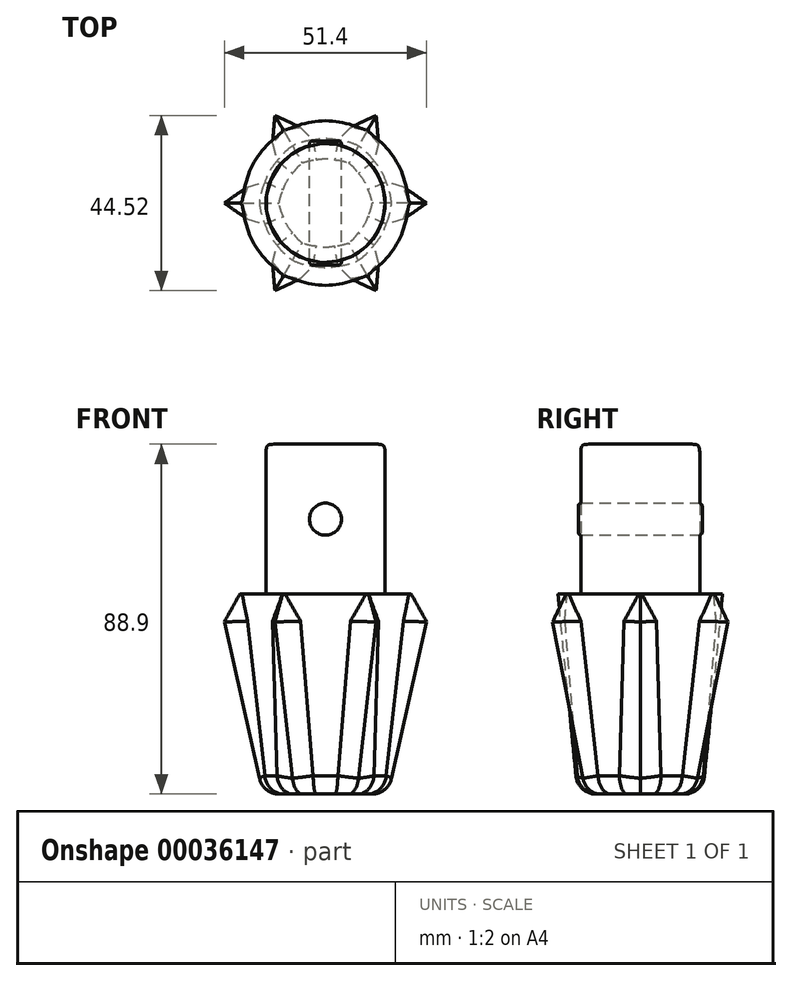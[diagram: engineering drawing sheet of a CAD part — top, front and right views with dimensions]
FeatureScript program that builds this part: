
annotation { "Feature Type Name" : "Feature", "Feature Type Description" : "" }
export const myFeature = defineFeature(function(context is Context, id is Id, definition is map)
    precondition{}
    {
        {
            var Q0;
            Q0=qCreatedBy(makeId("Top.planeOp"),FACE);
            cPlane(context, id + "F0", {"entities" : qUnion([Q0]), "cplaneType" : CPlaneType.OFFSET, "offset" : 50.8 * mm, "width" : 152.4 * mm, "height" : 152.4 * mm});
        }
        {
            var Q0;
            Q0=qCreatedBy(id+"F0.planeOp",FACE);
            var sketch = newSketch(context, id + "F1", { "sketchPlane" : qUnion([Q0])});
            skCircle(sketch, "E0.cCircle", {"center": v(0, 0) * mm, "radius": 27.3 * mm, "construction": true});
            skLineSegment(sketch, "E0.0", {"start": v(13.65, 23.64) * mm, "end": v(13.65, 15.82) * mm});
            skLineSegment(sketch, "E0.1", {"start": v(13.65, -23.64) * mm, "end": v(6.88, -19.73) * mm});
            skLineSegment(sketch, "E0.2", {"start": v(-27.3, 0) * mm, "end": v(-20.53, 3.9) * mm});
            skLineSegment(sketch, "E1.0", {"start": v(-13.65, 23.64) * mm, "end": v(-6.88, 19.73) * mm});
            skLineSegment(sketch, "E1.1", {"start": v(27.3, 0) * mm, "end": v(20.53, -3.9) * mm});
            skLineSegment(sketch, "E1.2", {"start": v(-13.65, -23.64) * mm, "end": v(-13.65, -15.82) * mm});
            skArc(sketch, "E2", {"start": v(-13.65, 15.82) * mm, "mid": v(-18.1, 10.45) * mm, "end": v(-20.53, 3.9) * mm});
            skLineSegment(sketch, "E3.trimOffspring", {"start": v(20.53, 3.9) * mm, "end": v(27.3, 0) * mm});
            skLineSegment(sketch, "E4.trimOffspring", {"start": v(-13.65, 15.82) * mm, "end": v(-13.65, 23.64) * mm});
            skLineSegment(sketch, "E5.trimOffspring", {"start": v(6.88, 19.73) * mm, "end": v(13.65, 23.64) * mm});
            skArc(sketch, "E6.trimOffspring", {"start": v(-20.53, -3.9) * mm, "mid": v(-18.1, -10.45) * mm, "end": v(-13.65, -15.82) * mm});
            skLineSegment(sketch, "E7.trimOffspring", {"start": v(-20.53, -3.9) * mm, "end": v(-27.3, 0) * mm});
            skArc(sketch, "E8.trimOffspring", {"start": v(-6.88, -19.73) * mm, "mid": v(0, -20.9) * mm, "end": v(6.88, -19.73) * mm});
            skArc(sketch, "E9.trimOffspring", {"start": v(13.65, -15.82) * mm, "mid": v(18.1, -10.45) * mm, "end": v(20.53, -3.9) * mm});
            skArc(sketch, "E10.trimOffspring", {"start": v(20.53, 3.9) * mm, "mid": v(18.1, 10.45) * mm, "end": v(13.65, 15.82) * mm});
            skArc(sketch, "E11.trimOffspring", {"start": v(6.88, 19.73) * mm, "mid": v(0, 20.9) * mm, "end": v(-6.88, 19.73) * mm});
            skLineSegment(sketch, "E12.trimOffspring", {"start": v(13.65, -15.82) * mm, "end": v(13.65, -23.64) * mm});
            skLineSegment(sketch, "E13.trimOffspring", {"start": v(-6.88, -19.73) * mm, "end": v(-13.65, -23.64) * mm});
            skSolve(sketch);
        }
        {
            var Q0;
            Q0=qCreatedBy(makeId("Top.planeOp"),FACE);
            var sketch = newSketch(context, id + "F2", { "sketchPlane" : qUnion([Q0])});
            skCircle(sketch, "E14", {"center": v(0, 0) * mm, "radius": 15.88 * mm});
            skSolve(sketch);
        }
        {
            var Q0;
            Q0=makeQuery(id+"F1.imprint","IMPRINT",FACE,{"disambiguationData":[TD([[makeQuery(id+"F1.imprint","IMPRINT",EDGE,{"derivedFrom":sQuery(id+"F1.wireOp",EDGE,"E0.0")}),-1.0]])]});
            var Q1;
            Q1=makeQuery(id+"F2.imprint","IMPRINT",FACE,{"disambiguationData":[TD([[makeQuery(id+"F2.imprint","IMPRINT",EDGE,{"derivedFrom":sQuery(id+"F2.wireOp",EDGE,"E14")}),1.0]])]});
            loft(context, id + "F3", {"sheetProfilesArray" : [{ "sheetProfileEntities" : qUnion([Q0]) }, { "sheetProfileEntities" : qUnion([Q1]) }]});
        }
        {
            var Q0;
            Q0=makeQuery(id+"F3.opLoft","CAP_FACE",FACE,{"disambiguationData":[OSD([makeQuery(id+"F2.imprint","IMPRINT",FACE,{"disambiguationData":[TD([[makeQuery(id+"F2.imprint","IMPRINT",EDGE,{"derivedFrom":sQuery(id+"F2.wireOp",EDGE,"E14")}),1.0]])]})])],"isStart":true});
            fillet(context, id + "F4", {"entities" : qUnion([Q0]), "radius" : 5.08 * mm, "tangentPropagation" : true, "allowEdgeOverflow" : false});
        }
        {
            var Q0;
            Q0=makeQuery(id+"F3.opLoft","MID_CAP_EDGE",EDGE,{"disambiguationData":[OSD([sQuery(id+"F1.wireOp",EDGE,"E0.1"),sQuery(id+"F1.wireOp",EDGE,"E9.trimOffspring"),sQuery(id+"F1.wireOp",EDGE,"E12.trimOffspring")])],"capPos":0.0});
            var Q1;
            Q1=makeQuery(id+"F3.opLoft","MID_CAP_EDGE",EDGE,{"disambiguationData":[OSD([sQuery(id+"F1.wireOp",EDGE,"E0.1"),sQuery(id+"F1.wireOp",EDGE,"E8.trimOffspring"),sQuery(id+"F1.wireOp",EDGE,"E12.trimOffspring")])],"capPos":0.0});
            var Q2;
            Q2=makeQuery(id+"F3.opLoft","MID_CAP_EDGE",EDGE,{"disambiguationData":[OSD([sQuery(id+"F1.wireOp",EDGE,"E1.1"),sQuery(id+"F1.wireOp",EDGE,"E3.trimOffspring"),sQuery(id+"F1.wireOp",EDGE,"E9.trimOffspring")])],"capPos":0.0});
            var Q3;
            Q3=makeQuery(id+"F3.opLoft","MID_CAP_EDGE",EDGE,{"disambiguationData":[OSD([sQuery(id+"F1.wireOp",EDGE,"E1.1"),sQuery(id+"F1.wireOp",EDGE,"E3.trimOffspring"),sQuery(id+"F1.wireOp",EDGE,"E10.trimOffspring")])],"capPos":0.0});
            var Q4;
            Q4=makeQuery(id+"F3.opLoft","MID_CAP_EDGE",EDGE,{"disambiguationData":[OSD([sQuery(id+"F1.wireOp",EDGE,"E0.0"),sQuery(id+"F1.wireOp",EDGE,"E5.trimOffspring"),sQuery(id+"F1.wireOp",EDGE,"E11.trimOffspring")])],"capPos":0.0});
            var Q5;
            Q5=makeQuery(id+"F3.opLoft","MID_CAP_EDGE",EDGE,{"disambiguationData":[OSD([sQuery(id+"F1.wireOp",EDGE,"E1.0"),sQuery(id+"F1.wireOp",EDGE,"E2"),sQuery(id+"F1.wireOp",EDGE,"E4.trimOffspring")])],"capPos":0.0});
            var Q6;
            Q6=makeQuery(id+"F3.opLoft","MID_CAP_EDGE",EDGE,{"disambiguationData":[OSD([sQuery(id+"F1.wireOp",EDGE,"E1.0"),sQuery(id+"F1.wireOp",EDGE,"E4.trimOffspring"),sQuery(id+"F1.wireOp",EDGE,"E11.trimOffspring")])],"capPos":0.0});
            var Q7;
            Q7=makeQuery(id+"F3.opLoft","MID_CAP_EDGE",EDGE,{"disambiguationData":[OSD([sQuery(id+"F1.wireOp",EDGE,"E0.0"),sQuery(id+"F1.wireOp",EDGE,"E5.trimOffspring"),sQuery(id+"F1.wireOp",EDGE,"E10.trimOffspring")])],"capPos":0.0});
            var Q8;
            Q8=makeQuery(id+"F3.opLoft","MID_CAP_EDGE",EDGE,{"disambiguationData":[OSD([sQuery(id+"F1.wireOp",EDGE,"E0.2"),sQuery(id+"F1.wireOp",EDGE,"E2"),sQuery(id+"F1.wireOp",EDGE,"E7.trimOffspring")])],"capPos":0.0});
            var Q9;
            Q9=makeQuery(id+"F3.opLoft","MID_CAP_EDGE",EDGE,{"disambiguationData":[OSD([sQuery(id+"F1.wireOp",EDGE,"E0.2"),sQuery(id+"F1.wireOp",EDGE,"E6.trimOffspring"),sQuery(id+"F1.wireOp",EDGE,"E7.trimOffspring")])],"capPos":0.0});
            var Q10;
            Q10=makeQuery(id+"F3.opLoft","MID_CAP_EDGE",EDGE,{"disambiguationData":[OSD([sQuery(id+"F1.wireOp",EDGE,"E1.2"),sQuery(id+"F1.wireOp",EDGE,"E6.trimOffspring"),sQuery(id+"F1.wireOp",EDGE,"E13.trimOffspring")])],"capPos":0.0});
            var Q11;
            Q11=makeQuery(id+"F3.opLoft","MID_CAP_EDGE",EDGE,{"disambiguationData":[OSD([sQuery(id+"F1.wireOp",EDGE,"E1.2"),sQuery(id+"F1.wireOp",EDGE,"E8.trimOffspring"),sQuery(id+"F1.wireOp",EDGE,"E13.trimOffspring")])],"capPos":0.0});
            chamfer(context, id + "F5", {"entities" : qUnion([Q0, Q1, Q2, Q3, Q4, Q5, Q6, Q7, Q8, Q9, Q10, Q11]), "chamferType" : ChamferType.OFFSET_ANGLE, "width" : 6.86 * mm, "oppositeDirection" : false, "angle" : 20 * degree, "tangentPropagation" : true});
        }
        {
            var Q0;
            Q0=makeQuery(id+"F3.opLoft","CAP_FACE",FACE,{"disambiguationData":[OSD([makeQuery(id+"F1.imprint","IMPRINT",FACE,{"disambiguationData":[TD([[makeQuery(id+"F1.imprint","IMPRINT",EDGE,{"derivedFrom":sQuery(id+"F1.wireOp",EDGE,"E0.0")}),-1.0]])]})])],"isStart":true});
            var sketch = newSketch(context, id + "F6", { "sketchPlane" : qUnion([Q0])});
            skCircle(sketch, "E15", {"center": v(0, 0) * mm, "radius": 15.11 * mm});
            skSolve(sketch);
        }
        {
            var Q0;
            Q0=makeQuery(id+"F6.imprint","IMPRINT",FACE,{"disambiguationData":[TD([[makeQuery(id+"F6.imprint","IMPRINT",EDGE,{"derivedFrom":sQuery(id+"F6.wireOp",EDGE,"E15")}),1.0]])]});
            extrude(context, id + "F7", {"entities" : qUnion([Q0]), "operationType" : NewBodyOperationType.ADD, "depth" : 38.1 * mm});
        }
        {
            var Q0;
            Q0=makeQuery(id+"F7.opExtrude","CAP_EDGE",EDGE,{"disambiguationData":[OSD([sQuery(id+"F6.wireOp",EDGE,"E15")])],"isStart":false});
            fillet(context, id + "F8", {"entities" : qUnion([Q0]), "radius" : 2.54 * mm, "tangentPropagation" : true, "rho" : 0.7, "crossSection" : FilletCrossSection.CONIC, "allowEdgeOverflow" : false});
        }
        {
            var Q0;
            Q0=qCreatedBy(makeId("Front.planeOp"),FACE);
            var sketch = newSketch(context, id + "F9", { "sketchPlane" : qUnion([Q0])});
            skCircle(sketch, "E16", {"center": v(0, 69.85) * mm, "radius": 4.06 * mm});
            skSolve(sketch);
        }
        {
            var Q0;
            Q0 = qSketchRegion(id + "F9", true);
            var Q1;
            Q1=sQuery(id+"F9.wireOp",EDGE,"E16");
            extrude(context, id + "F10", {"entities" : qUnion([Q0]), "surfaceEntities" : qUnion([Q1]), "depth" : 15.75 * mm, "hasSecondDirection" : true, "secondDirectionOppositeDirection" : true, "secondDirectionDepth" : 15.75 * mm});
        }
        {
            var Q0;
            Q0=makeQuery(id+"F10.opExtrude","CAP_EDGE",EDGE,{"disambiguationData":[OSD([sQuery(id+"F9.wireOp",EDGE,"E16")])],"isStart":true});
            var Q1;
            Q1=makeQuery(id+"F10.opExtrude","CAP_EDGE",EDGE,{"disambiguationData":[OSD([sQuery(id+"F9.wireOp",EDGE,"E16")])],"isStart":false});
            fillet(context, id + "F11", {"entities" : qUnion([Q0, Q1]), "radius" : 0.76 * mm, "tangentPropagation" : true, "allowEdgeOverflow" : false});
        }
    });
